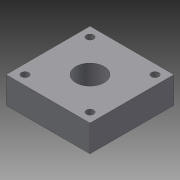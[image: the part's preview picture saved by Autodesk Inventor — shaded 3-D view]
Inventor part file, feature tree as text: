
AUTODESK INVENTOR PART (.ipt)
format: ipt  version: 2015 (Build 190159000, 159)  size: 93,184 bytes
history: native  units: in
note: dims shown in document units (in); Inventor stores cm internally (conversion verified against a paired STEP export)
features: extrude x2, sketch x2
ambient origin geometry x8: Origin, YZ Plane, XZ Plane, XY Plane, X Axis, Y Axis, Z Axis, Center Point
bodies: Body1 (feature_tree)
feature tree (4):
  extrude  "Extrusion2"  Depth=1.5748in
  extrude  "Extrusion3"  Depth=0.5in TaperAngle=0.0deg
  sketch  "Sketch1"  dims[d3=1.5748in d4=1.5748in]
  sketch  "Sketch2"  dims[d5=0.1378in d6=0.5in d7=0.0in d8=0.5in d9=0.0in d10=1.2205in d11=1.2205in d12=0.5315in]
